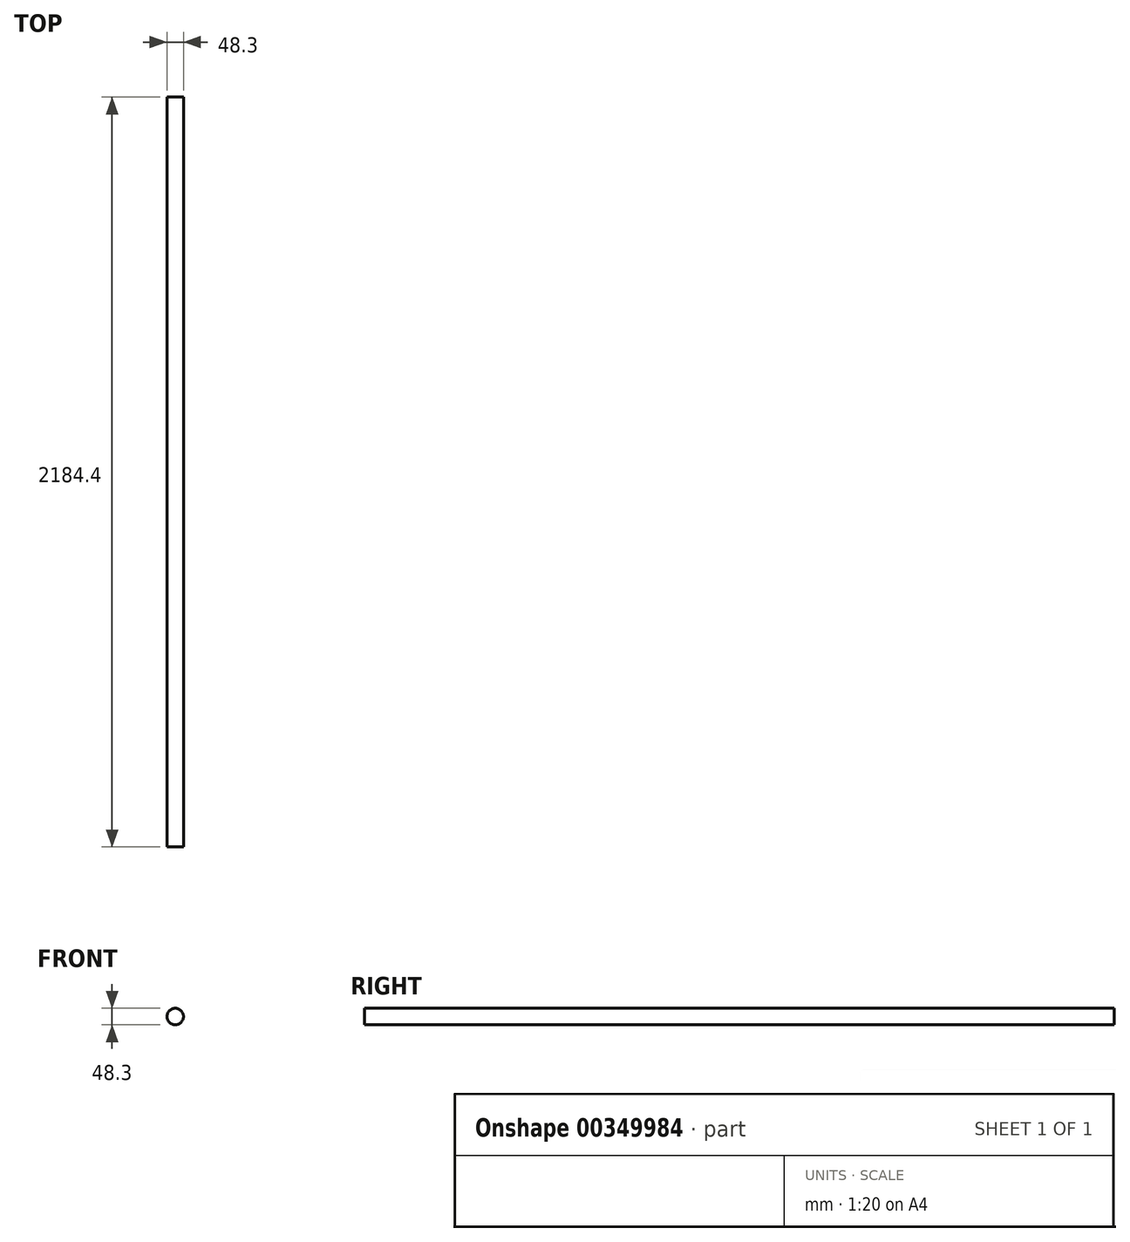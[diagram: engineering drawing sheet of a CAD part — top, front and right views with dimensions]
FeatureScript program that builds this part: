
annotation { "Feature Type Name" : "Feature", "Feature Type Description" : "" }
export const myFeature = defineFeature(function(context is Context, id is Id, definition is map)
    precondition{}
    {
        {
            var Q0;
            Q0=qCreatedBy(makeId("Front.planeOp"),FACE);
            var sketch = newSketch(context, id + "F0", { "sketchPlane" : qUnion([Q0])});
            skCircle(sketch, "E0", {"center": v(0, 0) * mm, "radius": 24.15 * mm});
            skSolve(sketch);
        }
        {
            var Q0;
            Q0 = qSketchRegion(id + "F0", true);
            extrude(context, id + "F1", {"entities" : qUnion([Q0]), "depth" : 2184.4 * mm, "offsetDistance" : 25.4 * mm});
        }
    });
